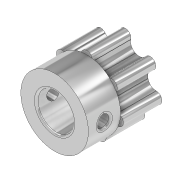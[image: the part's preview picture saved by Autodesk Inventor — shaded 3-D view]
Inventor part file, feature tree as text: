
AUTODESK INVENTOR PART (.ipt)
format: ipt  version: 2020 (Build 240168000, 168)  size: 309,760 bytes
history: native  units: in
note: dims shown in document units (in); Inventor stores cm internally (conversion verified against a paired STEP export)
features: extrude x3, sketch x3, chamfer x1, fillet x1
ambient origin geometry x8: Origin, YZ Plane, XZ Plane, XY Plane, X Axis, Y Axis, Z Axis, Center Point
bodies: Solid1 (feature_tree)
feature tree (8):
  extrude  "Extrusion1"  Depth=0.4724in
  extrude  "Extrusion2"  Depth=0.084in
  extrude  "Extrusion3"  Depth=0.084in
  chamfer  "Chamfer1"  Distance=2.7559in Angle=360.0deg
  fillet  "Fillet1"  Radius=0.2362in
  sketch  "Sketch1"  dims[d0=0.2047in d1=0.4724in]
  sketch  "Sketch2"  dims[d2=0.0866in d5=0.084in]
  sketch  "Sketch3"  dims[d6=0.084in d7=0.084in d8=2.7559in d10=360.0deg d12=0.2362in d13=0.0in d14=0.1969in d15=0.0in d16=0.0748in d17=0.1575in d18=0.0in d19=0.2756in d20=0.125in d21=0.0137in d22=0.0118in d23=0.0079in d24=0.4134in d25=0.0344in d26=0.5in d27=0.0344in]
